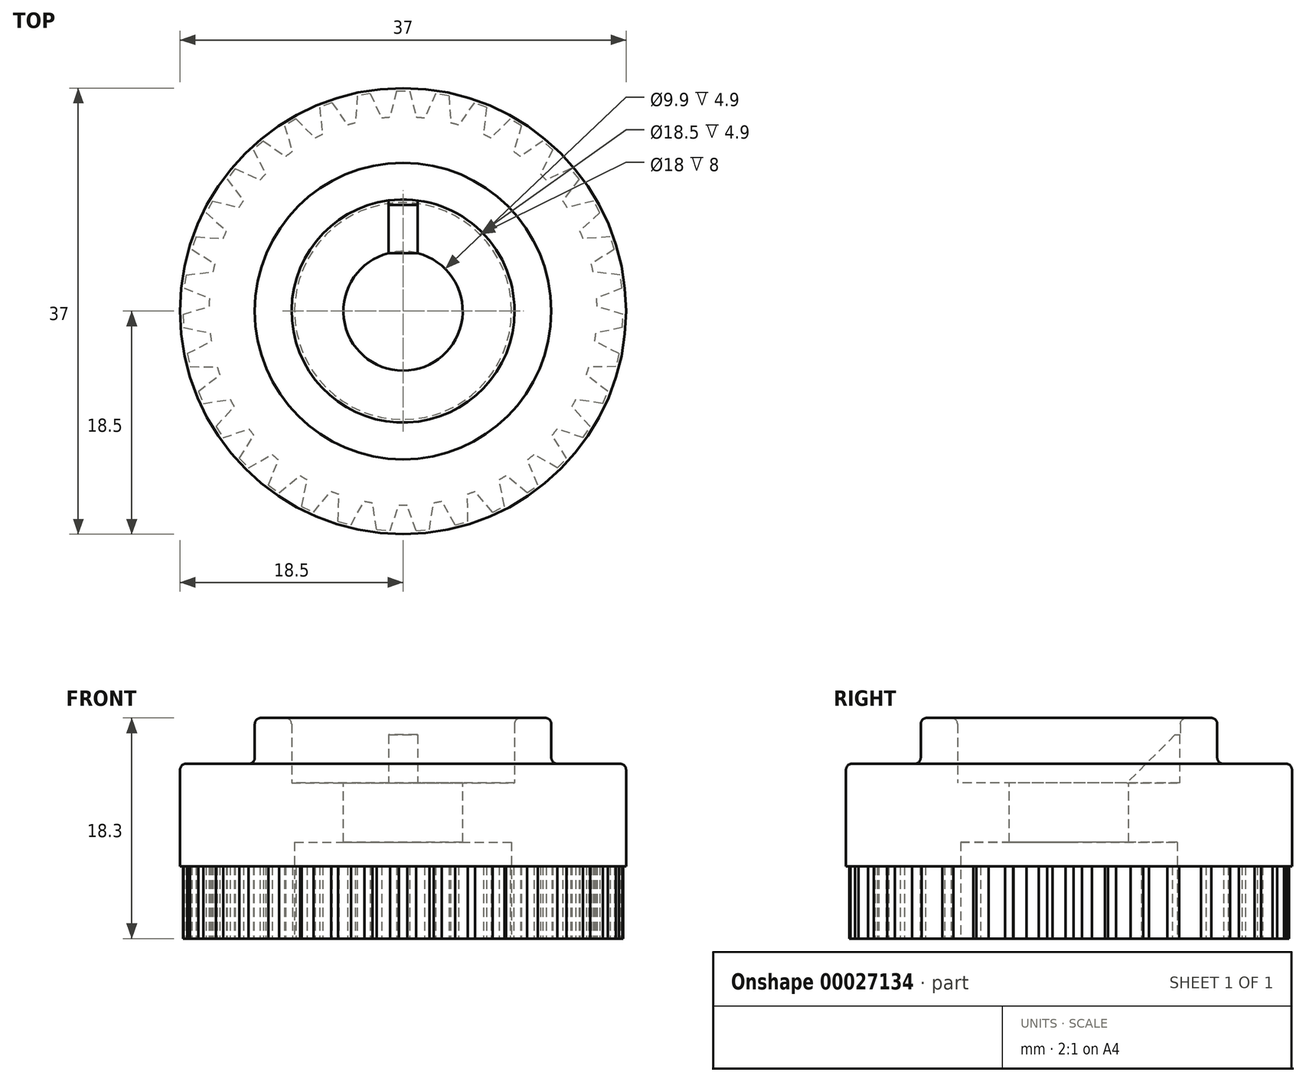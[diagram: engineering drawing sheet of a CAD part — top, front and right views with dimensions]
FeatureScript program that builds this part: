
annotation { "Feature Type Name" : "Feature", "Feature Type Description" : "" }
export const myFeature = defineFeature(function(context is Context, id is Id, definition is map)
    precondition{}
    {
        {
            var Q0;
            Q0=qCreatedBy(makeId("Top.planeOp"),FACE);
            var sketch = newSketch(context, id + "F0", { "sketchPlane" : qUnion([Q0])});
            skCircle(sketch, "E0", {"center": v(0, 0) * mm, "radius": 16.1 * mm});
            skLineSegment(sketch, "E1", {"start": v(0, 18.25) * mm, "end": v(0.55, 18.25) * mm});
            skLineSegment(sketch, "E2", {"start": v(0.55, 18.25) * mm, "end": v(1.1, 16.06) * mm});
            skLineSegment(sketch, "E3.MirrorCS", {"start": v(0, 18.25) * mm, "end": v(-0.55, 18.25) * mm});
            skLineSegment(sketch, "E4.MirrorCS", {"start": v(-0.55, 18.25) * mm, "end": v(-1.1, 16.06) * mm});
            skLineSegment(sketch, "E5.1.0", {"start": v(-3.26, 17.96) * mm, "end": v(-3.8, 17.86) * mm});
            skLineSegment(sketch, "E5.1.1", {"start": v(-3.26, 17.96) * mm, "end": v(-2.72, 18.05) * mm});
            skLineSegment(sketch, "E5.1.2", {"start": v(-3.8, 17.86) * mm, "end": v(-3.95, 15.6) * mm});
            skLineSegment(sketch, "E5.1.3", {"start": v(-2.72, 18.05) * mm, "end": v(-1.79, 16) * mm});
            skLineSegment(sketch, "E5.2.0", {"start": v(-6.41, 17.09) * mm, "end": v(-6.93, 16.9) * mm});
            skLineSegment(sketch, "E5.2.1", {"start": v(-6.41, 17.09) * mm, "end": v(-5.9, 17.28) * mm});
            skLineSegment(sketch, "E5.2.2", {"start": v(-6.93, 16.9) * mm, "end": v(-6.67, 14.65) * mm});
            skLineSegment(sketch, "E5.2.3", {"start": v(-5.9, 17.28) * mm, "end": v(-4.61, 15.42) * mm});
            skLineSegment(sketch, "E6.2.3.0", {"start": v(-9.36, 15.67) * mm, "end": v(-9.83, 15.38) * mm});
            skLineSegment(sketch, "E6.3.3.0", {"start": v(-9.36, 15.67) * mm, "end": v(-8.89, 15.95) * mm});
            skLineSegment(sketch, "E6.6.3.0", {"start": v(-9.83, 15.38) * mm, "end": v(-9.18, 13.22) * mm});
            skLineSegment(sketch, "E6.9.3.0", {"start": v(-8.89, 15.95) * mm, "end": v(-7.3, 14.35) * mm});
            skLineSegment(sketch, "E6.2.4.0", {"start": v(-12, 13.74) * mm, "end": v(-12.42, 13.38) * mm});
            skLineSegment(sketch, "E6.3.4.0", {"start": v(-12, 13.74) * mm, "end": v(-11.6, 14.1) * mm});
            skLineSegment(sketch, "E6.6.4.0", {"start": v(-12.42, 13.38) * mm, "end": v(-11.4, 11.37) * mm});
            skLineSegment(sketch, "E6.9.4.0", {"start": v(-11.6, 14.1) * mm, "end": v(-9.74, 12.82) * mm});
            skLineSegment(sketch, "E6.2.5.0", {"start": v(-14.27, 11.38) * mm, "end": v(-14.61, 10.95) * mm});
            skLineSegment(sketch, "E6.3.5.0", {"start": v(-14.27, 11.38) * mm, "end": v(-13.93, 11.8) * mm});
            skLineSegment(sketch, "E6.6.5.0", {"start": v(-14.61, 10.95) * mm, "end": v(-13.24, 9.15) * mm});
            skLineSegment(sketch, "E6.9.5.0", {"start": v(-13.93, 11.8) * mm, "end": v(-11.87, 10.87) * mm});
            skLineSegment(sketch, "E6.2.6.0", {"start": v(-16.07, 8.65) * mm, "end": v(-16.33, 8.16) * mm});
            skLineSegment(sketch, "E6.3.6.0", {"start": v(-16.07, 8.65) * mm, "end": v(-15.81, 9.13) * mm});
            skLineSegment(sketch, "E6.6.6.0", {"start": v(-16.33, 8.16) * mm, "end": v(-14.67, 6.64) * mm});
            skLineSegment(sketch, "E6.9.6.0", {"start": v(-15.81, 9.13) * mm, "end": v(-13.62, 8.58) * mm});
            skLineSegment(sketch, "E6.2.7.0", {"start": v(-17.36, 5.64) * mm, "end": v(-17.53, 5.12) * mm});
            skLineSegment(sketch, "E6.3.7.0", {"start": v(-17.36, 5.64) * mm, "end": v(-17.19, 6.16) * mm});
            skLineSegment(sketch, "E6.6.7.0", {"start": v(-17.53, 5.12) * mm, "end": v(-15.62, 3.92) * mm});
            skLineSegment(sketch, "E6.9.7.0", {"start": v(-17.19, 6.16) * mm, "end": v(-14.94, 6) * mm});
            skLineSegment(sketch, "E6.2.8.0", {"start": v(-18.08, 2.45) * mm, "end": v(-18.16, 1.9) * mm});
            skLineSegment(sketch, "E6.3.8.0", {"start": v(-18.08, 2.45) * mm, "end": v(-18.01, 3) * mm});
            skLineSegment(sketch, "E6.6.8.0", {"start": v(-18.16, 1.9) * mm, "end": v(-16.06, 1.07) * mm});
            skLineSegment(sketch, "E6.9.8.0", {"start": v(-18.01, 3) * mm, "end": v(-15.77, 3.25) * mm});
            skLineSegment(sketch, "E6.2.9.0", {"start": v(-18.23, -0.82) * mm, "end": v(-18.2, -1.37) * mm});
            skLineSegment(sketch, "E6.3.9.0", {"start": v(-18.23, -0.82) * mm, "end": v(-18.26, -0.27) * mm});
            skLineSegment(sketch, "E6.6.9.0", {"start": v(-18.2, -1.37) * mm, "end": v(-16, -1.82) * mm});
            skLineSegment(sketch, "E6.9.9.0", {"start": v(-18.26, -0.27) * mm, "end": v(-16.1, 0.38) * mm});
            skLineSegment(sketch, "E6.2.10.0", {"start": v(-17.8, -4.06) * mm, "end": v(-17.67, -4.6) * mm});
            skLineSegment(sketch, "E6.3.10.0", {"start": v(-17.8, -4.06) * mm, "end": v(-17.91, -3.52) * mm});
            skLineSegment(sketch, "E6.6.10.0", {"start": v(-17.67, -4.6) * mm, "end": v(-15.41, -4.65) * mm});
            skLineSegment(sketch, "E6.9.10.0", {"start": v(-17.91, -3.52) * mm, "end": v(-15.9, -2.5) * mm});
            skLineSegment(sketch, "E6.2.11.0", {"start": v(-16.78, -7.17) * mm, "end": v(-16.57, -7.68) * mm});
            skLineSegment(sketch, "E6.3.11.0", {"start": v(-16.78, -7.17) * mm, "end": v(-17, -6.67) * mm});
            skLineSegment(sketch, "E6.6.11.0", {"start": v(-16.57, -7.68) * mm, "end": v(-14.34, -7.32) * mm});
            skLineSegment(sketch, "E6.9.11.0", {"start": v(-17, -6.67) * mm, "end": v(-15.2, -5.3) * mm});
            skLineSegment(sketch, "E6.2.12.0", {"start": v(-15.23, -10.05) * mm, "end": v(-14.93, -10.51) * mm});
            skLineSegment(sketch, "E6.3.12.0", {"start": v(-15.23, -10.05) * mm, "end": v(-15.53, -9.6) * mm});
            skLineSegment(sketch, "E6.6.12.0", {"start": v(-14.93, -10.51) * mm, "end": v(-12.8, -9.77) * mm});
            skLineSegment(sketch, "E6.9.12.0", {"start": v(-15.53, -9.6) * mm, "end": v(-14.01, -7.93) * mm});
            skLineSegment(sketch, "E6.2.13.0", {"start": v(-13.2, -12.61) * mm, "end": v(-12.81, -13) * mm});
            skLineSegment(sketch, "E6.3.13.0", {"start": v(-13.2, -12.61) * mm, "end": v(-13.57, -12.21) * mm});
            skLineSegment(sketch, "E6.6.13.0", {"start": v(-12.81, -13) * mm, "end": v(-10.85, -11.9) * mm});
            skLineSegment(sketch, "E6.9.13.0", {"start": v(-13.57, -12.21) * mm, "end": v(-12.37, -10.3) * mm});
            skLineSegment(sketch, "E6.2.14.0", {"start": v(-10.73, -14.76) * mm, "end": v(-10.28, -15.09) * mm});
            skLineSegment(sketch, "E6.3.14.0", {"start": v(-10.73, -14.76) * mm, "end": v(-11.17, -14.44) * mm});
            skLineSegment(sketch, "E6.6.14.0", {"start": v(-10.28, -15.09) * mm, "end": v(-8.55, -13.64) * mm});
            skLineSegment(sketch, "E6.9.14.0", {"start": v(-11.17, -14.44) * mm, "end": v(-10.33, -12.35) * mm});
            skLineSegment(sketch, "E6.2.15.0", {"start": v(-7.92, -16.44) * mm, "end": v(-7.42, -16.68) * mm});
            skLineSegment(sketch, "E6.3.15.0", {"start": v(-7.92, -16.44) * mm, "end": v(-8.41, -16.2) * mm});
            skLineSegment(sketch, "E6.6.15.0", {"start": v(-7.42, -16.68) * mm, "end": v(-5.98, -14.95) * mm});
            skLineSegment(sketch, "E6.9.15.0", {"start": v(-8.41, -16.2) * mm, "end": v(-7.96, -14) * mm});
            skLineSegment(sketch, "E6.2.16.0", {"start": v(-4.86, -17.6) * mm, "end": v(-4.32, -17.74) * mm});
            skLineSegment(sketch, "E6.3.16.0", {"start": v(-4.86, -17.6) * mm, "end": v(-5.39, -17.45) * mm});
            skLineSegment(sketch, "E6.6.16.0", {"start": v(-4.32, -17.74) * mm, "end": v(-3.21, -15.78) * mm});
            skLineSegment(sketch, "E6.9.16.0", {"start": v(-5.39, -17.45) * mm, "end": v(-5.33, -15.2) * mm});
            skLineSegment(sketch, "E6.2.17.0", {"start": v(-1.64, -18.18) * mm, "end": v(-1.09, -18.23) * mm});
            skLineSegment(sketch, "E6.3.17.0", {"start": v(-1.64, -18.18) * mm, "end": v(-2.18, -18.13) * mm});
            skLineSegment(sketch, "E6.6.17.0", {"start": v(-1.09, -18.23) * mm, "end": v(-0.34, -16.1) * mm});
            skLineSegment(sketch, "E6.9.17.0", {"start": v(-2.18, -18.13) * mm, "end": v(-2.54, -15.9) * mm});
            skLineSegment(sketch, "E6.2.18.0", {"start": v(1.64, -18.18) * mm, "end": v(2.18, -18.13) * mm});
            skLineSegment(sketch, "E6.3.18.0", {"start": v(1.64, -18.18) * mm, "end": v(1.09, -18.23) * mm});
            skLineSegment(sketch, "E6.6.18.0", {"start": v(2.18, -18.13) * mm, "end": v(2.54, -15.9) * mm});
            skLineSegment(sketch, "E6.9.18.0", {"start": v(1.09, -18.23) * mm, "end": v(0.34, -16.1) * mm});
            skLineSegment(sketch, "E6.2.19.0", {"start": v(4.86, -17.6) * mm, "end": v(5.39, -17.45) * mm});
            skLineSegment(sketch, "E6.3.19.0", {"start": v(4.86, -17.6) * mm, "end": v(4.32, -17.74) * mm});
            skLineSegment(sketch, "E6.6.19.0", {"start": v(5.39, -17.45) * mm, "end": v(5.33, -15.2) * mm});
            skLineSegment(sketch, "E6.9.19.0", {"start": v(4.32, -17.74) * mm, "end": v(3.21, -15.78) * mm});
            skLineSegment(sketch, "E6.2.20.0", {"start": v(7.92, -16.44) * mm, "end": v(8.41, -16.2) * mm});
            skLineSegment(sketch, "E6.3.20.0", {"start": v(7.92, -16.44) * mm, "end": v(7.42, -16.68) * mm});
            skLineSegment(sketch, "E6.6.20.0", {"start": v(8.41, -16.2) * mm, "end": v(7.96, -14) * mm});
            skLineSegment(sketch, "E6.9.20.0", {"start": v(7.42, -16.68) * mm, "end": v(5.98, -14.95) * mm});
            skLineSegment(sketch, "E6.2.21.0", {"start": v(10.73, -14.76) * mm, "end": v(11.17, -14.44) * mm});
            skLineSegment(sketch, "E6.3.21.0", {"start": v(10.73, -14.76) * mm, "end": v(10.28, -15.09) * mm});
            skLineSegment(sketch, "E6.6.21.0", {"start": v(11.17, -14.44) * mm, "end": v(10.33, -12.35) * mm});
            skLineSegment(sketch, "E6.9.21.0", {"start": v(10.28, -15.09) * mm, "end": v(8.55, -13.64) * mm});
            skLineSegment(sketch, "E6.2.22.0", {"start": v(13.2, -12.61) * mm, "end": v(13.57, -12.21) * mm});
            skLineSegment(sketch, "E6.3.22.0", {"start": v(13.2, -12.61) * mm, "end": v(12.81, -13) * mm});
            skLineSegment(sketch, "E6.6.22.0", {"start": v(13.57, -12.21) * mm, "end": v(12.37, -10.3) * mm});
            skLineSegment(sketch, "E6.9.22.0", {"start": v(12.81, -13) * mm, "end": v(10.85, -11.9) * mm});
            skLineSegment(sketch, "E6.2.23.0", {"start": v(15.23, -10.05) * mm, "end": v(15.53, -9.6) * mm});
            skLineSegment(sketch, "E6.3.23.0", {"start": v(15.23, -10.05) * mm, "end": v(14.93, -10.51) * mm});
            skLineSegment(sketch, "E6.6.23.0", {"start": v(15.53, -9.6) * mm, "end": v(14.01, -7.93) * mm});
            skLineSegment(sketch, "E6.9.23.0", {"start": v(14.93, -10.51) * mm, "end": v(12.8, -9.77) * mm});
            skLineSegment(sketch, "E6.2.24.0", {"start": v(16.78, -7.17) * mm, "end": v(17, -6.67) * mm});
            skLineSegment(sketch, "E6.3.24.0", {"start": v(16.78, -7.17) * mm, "end": v(16.57, -7.68) * mm});
            skLineSegment(sketch, "E6.6.24.0", {"start": v(17, -6.67) * mm, "end": v(15.2, -5.3) * mm});
            skLineSegment(sketch, "E6.9.24.0", {"start": v(16.57, -7.68) * mm, "end": v(14.34, -7.32) * mm});
            skLineSegment(sketch, "E6.2.25.0", {"start": v(17.8, -4.06) * mm, "end": v(17.91, -3.52) * mm});
            skLineSegment(sketch, "E6.3.25.0", {"start": v(17.8, -4.06) * mm, "end": v(17.67, -4.6) * mm});
            skLineSegment(sketch, "E6.6.25.0", {"start": v(17.91, -3.52) * mm, "end": v(15.9, -2.5) * mm});
            skLineSegment(sketch, "E6.9.25.0", {"start": v(17.67, -4.6) * mm, "end": v(15.41, -4.65) * mm});
            skLineSegment(sketch, "E6.2.26.0", {"start": v(18.23, -0.82) * mm, "end": v(18.26, -0.27) * mm});
            skLineSegment(sketch, "E6.3.26.0", {"start": v(18.23, -0.82) * mm, "end": v(18.2, -1.37) * mm});
            skLineSegment(sketch, "E6.6.26.0", {"start": v(18.26, -0.27) * mm, "end": v(16.1, 0.38) * mm});
            skLineSegment(sketch, "E6.9.26.0", {"start": v(18.2, -1.37) * mm, "end": v(16, -1.82) * mm});
            skLineSegment(sketch, "E6.2.27.0", {"start": v(18.08, 2.45) * mm, "end": v(18.01, 3) * mm});
            skLineSegment(sketch, "E6.3.27.0", {"start": v(18.08, 2.45) * mm, "end": v(18.16, 1.9) * mm});
            skLineSegment(sketch, "E6.6.27.0", {"start": v(18.01, 3) * mm, "end": v(15.77, 3.25) * mm});
            skLineSegment(sketch, "E6.9.27.0", {"start": v(18.16, 1.9) * mm, "end": v(16.06, 1.07) * mm});
            skLineSegment(sketch, "E6.2.28.0", {"start": v(17.36, 5.64) * mm, "end": v(17.19, 6.16) * mm});
            skLineSegment(sketch, "E6.3.28.0", {"start": v(17.36, 5.64) * mm, "end": v(17.53, 5.12) * mm});
            skLineSegment(sketch, "E6.6.28.0", {"start": v(17.19, 6.16) * mm, "end": v(14.94, 6) * mm});
            skLineSegment(sketch, "E6.9.28.0", {"start": v(17.53, 5.12) * mm, "end": v(15.62, 3.92) * mm});
            skLineSegment(sketch, "E6.2.29.0", {"start": v(16.07, 8.65) * mm, "end": v(15.81, 9.13) * mm});
            skLineSegment(sketch, "E6.3.29.0", {"start": v(16.07, 8.65) * mm, "end": v(16.33, 8.16) * mm});
            skLineSegment(sketch, "E6.6.29.0", {"start": v(15.81, 9.13) * mm, "end": v(13.62, 8.58) * mm});
            skLineSegment(sketch, "E6.9.29.0", {"start": v(16.33, 8.16) * mm, "end": v(14.67, 6.64) * mm});
            skLineSegment(sketch, "E6.2.30.0", {"start": v(14.27, 11.38) * mm, "end": v(13.93, 11.8) * mm});
            skLineSegment(sketch, "E6.3.30.0", {"start": v(14.27, 11.38) * mm, "end": v(14.61, 10.95) * mm});
            skLineSegment(sketch, "E6.6.30.0", {"start": v(13.93, 11.8) * mm, "end": v(11.87, 10.87) * mm});
            skLineSegment(sketch, "E6.9.30.0", {"start": v(14.61, 10.95) * mm, "end": v(13.24, 9.15) * mm});
            skLineSegment(sketch, "E6.2.31.0", {"start": v(12, 13.74) * mm, "end": v(11.6, 14.1) * mm});
            skLineSegment(sketch, "E6.3.31.0", {"start": v(12, 13.74) * mm, "end": v(12.42, 13.38) * mm});
            skLineSegment(sketch, "E6.6.31.0", {"start": v(11.6, 14.1) * mm, "end": v(9.74, 12.82) * mm});
            skLineSegment(sketch, "E6.9.31.0", {"start": v(12.42, 13.38) * mm, "end": v(11.4, 11.37) * mm});
            skLineSegment(sketch, "E6.2.32.0", {"start": v(9.36, 15.67) * mm, "end": v(8.89, 15.95) * mm});
            skLineSegment(sketch, "E6.3.32.0", {"start": v(9.36, 15.67) * mm, "end": v(9.83, 15.38) * mm});
            skLineSegment(sketch, "E6.6.32.0", {"start": v(8.89, 15.95) * mm, "end": v(7.3, 14.35) * mm});
            skLineSegment(sketch, "E6.9.32.0", {"start": v(9.83, 15.38) * mm, "end": v(9.18, 13.22) * mm});
            skLineSegment(sketch, "E6.2.33.0", {"start": v(6.41, 17.09) * mm, "end": v(5.9, 17.28) * mm});
            skLineSegment(sketch, "E6.3.33.0", {"start": v(6.41, 17.09) * mm, "end": v(6.93, 16.9) * mm});
            skLineSegment(sketch, "E6.6.33.0", {"start": v(5.9, 17.28) * mm, "end": v(4.61, 15.42) * mm});
            skLineSegment(sketch, "E6.9.33.0", {"start": v(6.93, 16.9) * mm, "end": v(6.67, 14.65) * mm});
            skLineSegment(sketch, "E6.2.34.0", {"start": v(3.26, 17.96) * mm, "end": v(2.72, 18.05) * mm});
            skLineSegment(sketch, "E6.3.34.0", {"start": v(3.26, 17.96) * mm, "end": v(3.8, 17.86) * mm});
            skLineSegment(sketch, "E6.6.34.0", {"start": v(2.72, 18.05) * mm, "end": v(1.79, 16) * mm});
            skLineSegment(sketch, "E6.9.34.0", {"start": v(3.8, 17.86) * mm, "end": v(3.95, 15.6) * mm});
            skSolve(sketch);
        }
        {
            var Q0;
            Q0 = qSketchRegion(id + "F0", true);
            extrude(context, id + "F1", {"entities" : qUnion([Q0]), "depth" : 6 * mm});
        }
        {
            var Q0;
            Q0=makeQuery(id+"F1.opExtrude","CAP_FACE",FACE,{"disambiguationData":[OSD([sQuery(id+"F0.wireOp",EDGE,"E0"),sQuery(id+"F0.wireOp",EDGE,"E1"),sQuery(id+"F0.wireOp",EDGE,"E2"),sQuery(id+"F0.wireOp",EDGE,"E3.MirrorCS"),sQuery(id+"F0.wireOp",EDGE,"E4.MirrorCS"),sQuery(id+"F0.wireOp",EDGE,"E5.1.0"),sQuery(id+"F0.wireOp",EDGE,"E5.1.1"),sQuery(id+"F0.wireOp",EDGE,"E5.1.2"),sQuery(id+"F0.wireOp",EDGE,"E5.1.3"),sQuery(id+"F0.wireOp",EDGE,"E5.2.0"),sQuery(id+"F0.wireOp",EDGE,"E5.2.1"),sQuery(id+"F0.wireOp",EDGE,"E5.2.2"),sQuery(id+"F0.wireOp",EDGE,"E5.2.3"),sQuery(id+"F0.wireOp",EDGE,"E6.2.3.0"),sQuery(id+"F0.wireOp",EDGE,"E6.3.3.0"),sQuery(id+"F0.wireOp",EDGE,"E6.6.3.0"),sQuery(id+"F0.wireOp",EDGE,"E6.9.3.0"),sQuery(id+"F0.wireOp",EDGE,"E6.2.4.0"),sQuery(id+"F0.wireOp",EDGE,"E6.3.4.0"),sQuery(id+"F0.wireOp",EDGE,"E6.6.4.0"),sQuery(id+"F0.wireOp",EDGE,"E6.9.4.0"),sQuery(id+"F0.wireOp",EDGE,"E6.2.5.0"),sQuery(id+"F0.wireOp",EDGE,"E6.3.5.0"),sQuery(id+"F0.wireOp",EDGE,"E6.6.5.0"),sQuery(id+"F0.wireOp",EDGE,"E6.9.5.0"),sQuery(id+"F0.wireOp",EDGE,"E6.2.6.0"),sQuery(id+"F0.wireOp",EDGE,"E6.3.6.0"),sQuery(id+"F0.wireOp",EDGE,"E6.6.6.0"),sQuery(id+"F0.wireOp",EDGE,"E6.9.6.0"),sQuery(id+"F0.wireOp",EDGE,"E6.2.7.0"),sQuery(id+"F0.wireOp",EDGE,"E6.3.7.0"),sQuery(id+"F0.wireOp",EDGE,"E6.6.7.0"),sQuery(id+"F0.wireOp",EDGE,"E6.9.7.0"),sQuery(id+"F0.wireOp",EDGE,"E6.2.8.0"),sQuery(id+"F0.wireOp",EDGE,"E6.3.8.0"),sQuery(id+"F0.wireOp",EDGE,"E6.6.8.0"),sQuery(id+"F0.wireOp",EDGE,"E6.9.8.0"),sQuery(id+"F0.wireOp",EDGE,"E6.2.9.0"),sQuery(id+"F0.wireOp",EDGE,"E6.3.9.0"),sQuery(id+"F0.wireOp",EDGE,"E6.6.9.0"),sQuery(id+"F0.wireOp",EDGE,"E6.9.9.0"),sQuery(id+"F0.wireOp",EDGE,"E6.2.10.0"),sQuery(id+"F0.wireOp",EDGE,"E6.3.10.0"),sQuery(id+"F0.wireOp",EDGE,"E6.6.10.0"),sQuery(id+"F0.wireOp",EDGE,"E6.9.10.0"),sQuery(id+"F0.wireOp",EDGE,"E6.2.11.0"),sQuery(id+"F0.wireOp",EDGE,"E6.3.11.0"),sQuery(id+"F0.wireOp",EDGE,"E6.6.11.0"),sQuery(id+"F0.wireOp",EDGE,"E6.9.11.0"),sQuery(id+"F0.wireOp",EDGE,"E6.2.12.0"),sQuery(id+"F0.wireOp",EDGE,"E6.3.12.0"),sQuery(id+"F0.wireOp",EDGE,"E6.6.12.0"),sQuery(id+"F0.wireOp",EDGE,"E6.9.12.0"),sQuery(id+"F0.wireOp",EDGE,"E6.2.13.0"),sQuery(id+"F0.wireOp",EDGE,"E6.3.13.0"),sQuery(id+"F0.wireOp",EDGE,"E6.6.13.0"),sQuery(id+"F0.wireOp",EDGE,"E6.9.13.0"),sQuery(id+"F0.wireOp",EDGE,"E6.2.14.0"),sQuery(id+"F0.wireOp",EDGE,"E6.3.14.0"),sQuery(id+"F0.wireOp",EDGE,"E6.6.14.0"),sQuery(id+"F0.wireOp",EDGE,"E6.9.14.0"),sQuery(id+"F0.wireOp",EDGE,"E6.2.15.0"),sQuery(id+"F0.wireOp",EDGE,"E6.3.15.0"),sQuery(id+"F0.wireOp",EDGE,"E6.6.15.0"),sQuery(id+"F0.wireOp",EDGE,"E6.9.15.0"),sQuery(id+"F0.wireOp",EDGE,"E6.2.16.0"),sQuery(id+"F0.wireOp",EDGE,"E6.3.16.0"),sQuery(id+"F0.wireOp",EDGE,"E6.6.16.0"),sQuery(id+"F0.wireOp",EDGE,"E6.9.16.0"),sQuery(id+"F0.wireOp",EDGE,"E6.2.17.0"),sQuery(id+"F0.wireOp",EDGE,"E6.3.17.0"),sQuery(id+"F0.wireOp",EDGE,"E6.6.17.0"),sQuery(id+"F0.wireOp",EDGE,"E6.9.17.0"),sQuery(id+"F0.wireOp",EDGE,"E6.2.18.0"),sQuery(id+"F0.wireOp",EDGE,"E6.3.18.0"),sQuery(id+"F0.wireOp",EDGE,"E6.6.18.0"),sQuery(id+"F0.wireOp",EDGE,"E6.9.18.0"),sQuery(id+"F0.wireOp",EDGE,"E6.2.19.0"),sQuery(id+"F0.wireOp",EDGE,"E6.3.19.0"),sQuery(id+"F0.wireOp",EDGE,"E6.6.19.0"),sQuery(id+"F0.wireOp",EDGE,"E6.9.19.0"),sQuery(id+"F0.wireOp",EDGE,"E6.2.20.0"),sQuery(id+"F0.wireOp",EDGE,"E6.3.20.0"),sQuery(id+"F0.wireOp",EDGE,"E6.6.20.0"),sQuery(id+"F0.wireOp",EDGE,"E6.9.20.0"),sQuery(id+"F0.wireOp",EDGE,"E6.2.21.0"),sQuery(id+"F0.wireOp",EDGE,"E6.3.21.0"),sQuery(id+"F0.wireOp",EDGE,"E6.6.21.0"),sQuery(id+"F0.wireOp",EDGE,"E6.9.21.0"),sQuery(id+"F0.wireOp",EDGE,"E6.2.22.0"),sQuery(id+"F0.wireOp",EDGE,"E6.3.22.0"),sQuery(id+"F0.wireOp",EDGE,"E6.6.22.0"),sQuery(id+"F0.wireOp",EDGE,"E6.9.22.0"),sQuery(id+"F0.wireOp",EDGE,"E6.2.23.0"),sQuery(id+"F0.wireOp",EDGE,"E6.3.23.0"),sQuery(id+"F0.wireOp",EDGE,"E6.6.23.0"),sQuery(id+"F0.wireOp",EDGE,"E6.9.23.0"),sQuery(id+"F0.wireOp",EDGE,"E6.2.24.0"),sQuery(id+"F0.wireOp",EDGE,"E6.3.24.0"),sQuery(id+"F0.wireOp",EDGE,"E6.6.24.0"),sQuery(id+"F0.wireOp",EDGE,"E6.9.24.0"),sQuery(id+"F0.wireOp",EDGE,"E6.2.25.0"),sQuery(id+"F0.wireOp",EDGE,"E6.3.25.0"),sQuery(id+"F0.wireOp",EDGE,"E6.6.25.0"),sQuery(id+"F0.wireOp",EDGE,"E6.9.25.0"),sQuery(id+"F0.wireOp",EDGE,"E6.2.26.0"),sQuery(id+"F0.wireOp",EDGE,"E6.3.26.0"),sQuery(id+"F0.wireOp",EDGE,"E6.6.26.0"),sQuery(id+"F0.wireOp",EDGE,"E6.9.26.0"),sQuery(id+"F0.wireOp",EDGE,"E6.2.27.0"),sQuery(id+"F0.wireOp",EDGE,"E6.3.27.0"),sQuery(id+"F0.wireOp",EDGE,"E6.6.27.0"),sQuery(id+"F0.wireOp",EDGE,"E6.9.27.0"),sQuery(id+"F0.wireOp",EDGE,"E6.2.28.0"),sQuery(id+"F0.wireOp",EDGE,"E6.3.28.0"),sQuery(id+"F0.wireOp",EDGE,"E6.6.28.0"),sQuery(id+"F0.wireOp",EDGE,"E6.9.28.0"),sQuery(id+"F0.wireOp",EDGE,"E6.2.29.0"),sQuery(id+"F0.wireOp",EDGE,"E6.3.29.0"),sQuery(id+"F0.wireOp",EDGE,"E6.6.29.0"),sQuery(id+"F0.wireOp",EDGE,"E6.9.29.0"),sQuery(id+"F0.wireOp",EDGE,"E6.2.30.0"),sQuery(id+"F0.wireOp",EDGE,"E6.3.30.0"),sQuery(id+"F0.wireOp",EDGE,"E6.6.30.0"),sQuery(id+"F0.wireOp",EDGE,"E6.9.30.0"),sQuery(id+"F0.wireOp",EDGE,"E6.2.31.0"),sQuery(id+"F0.wireOp",EDGE,"E6.3.31.0"),sQuery(id+"F0.wireOp",EDGE,"E6.6.31.0"),sQuery(id+"F0.wireOp",EDGE,"E6.9.31.0"),sQuery(id+"F0.wireOp",EDGE,"E6.2.32.0"),sQuery(id+"F0.wireOp",EDGE,"E6.3.32.0"),sQuery(id+"F0.wireOp",EDGE,"E6.6.32.0"),sQuery(id+"F0.wireOp",EDGE,"E6.9.32.0"),sQuery(id+"F0.wireOp",EDGE,"E6.2.33.0"),sQuery(id+"F0.wireOp",EDGE,"E6.3.33.0"),sQuery(id+"F0.wireOp",EDGE,"E6.6.33.0"),sQuery(id+"F0.wireOp",EDGE,"E6.9.33.0"),sQuery(id+"F0.wireOp",EDGE,"E6.2.34.0"),sQuery(id+"F0.wireOp",EDGE,"E6.3.34.0"),sQuery(id+"F0.wireOp",EDGE,"E6.6.34.0"),sQuery(id+"F0.wireOp",EDGE,"E6.9.34.0")])],"isStart":false});
            var sketch = newSketch(context, id + "F2", { "sketchPlane" : qUnion([Q0])});
            skCircle(sketch, "E7", {"center": v(0, 0) * mm, "radius": 18.5 * mm});
            skSolve(sketch);
        }
        {
            var Q0;
            Q0 = qSketchRegion(id + "F2", true);
            extrude(context, id + "F3", {"entities" : qUnion([Q0]), "operationType" : NewBodyOperationType.ADD, "depth" : 8.5 * mm});
        }
        {
            var Q0;
            Q0=makeQuery(id+"F3.opExtrude","CAP_FACE",FACE,{"disambiguationData":[OSD([sQuery(id+"F2.wireOp",EDGE,"E7")])],"isStart":false});
            var sketch = newSketch(context, id + "F4", { "sketchPlane" : qUnion([Q0])});
            skCircle(sketch, "E8", {"center": v(0, 0) * mm, "radius": 12.3 * mm});
            skCircle(sketch, "E9", {"center": v(0, 0) * mm, "radius": 9.25 * mm});
            skSolve(sketch);
        }
        {
            var Q0;
            Q0 = qSketchRegion(id + "F4", true);
            extrude(context, id + "F5", {"entities" : qUnion([Q0]), "operationType" : NewBodyOperationType.ADD, "depth" : 3.8 * mm});
        }
        {
            var Q0;
            Q0=makeQuery(id+"F5.boolean.opBoolean","SPLIT",FACE,{"disambiguationData":[TD([makeQuery(id+"F5.opExtrude","SWEPT_FACE",FACE,{"disambiguationData":[OSD([sQuery(id+"F4.wireOp",EDGE,"E9")])]})])],"derivedFrom":makeQuery(id+"F3.opExtrude","CAP_FACE",FACE,{"disambiguationData":[OSD([sQuery(id+"F2.wireOp",EDGE,"E7")])],"isStart":false})});
            extrude(context, id + "F6", {"entities" : qUnion([Q0]), "operationType" : NewBodyOperationType.REMOVE, "oppositeDirection" : true, "depth" : 1.6 * mm});
        }
        {
            var Q0;
            Q0=makeQuery(id+"F6.boolean.opBoolean","COPY",FACE,{"derivedFrom":makeQuery(id+"F6.opExtrude","CAP_FACE",FACE,{"disambiguationData":[OSD([sQuery(id+"F2.wireOp",EDGE,"E7")])],"isStart":false})});
            var sketch = newSketch(context, id + "F7", { "sketchPlane" : qUnion([Q0])});
            skCircle(sketch, "E10", {"center": v(0, 0) * mm, "radius": 4.95 * mm});
            skSolve(sketch);
        }
        {
            var Q0;
            Q0 = qSketchRegion(id + "F7", true);
            extrude(context, id + "F8", {"entities" : qUnion([Q0]), "operationType" : NewBodyOperationType.REMOVE, "endBound" : BoundingType.UP_TO_NEXT, "oppositeDirection" : true, "depth" : 25 * mm});
        }
        {
            var Q0;
            Q0=makeQuery(id+"F6.boolean.opBoolean","COPY",FACE,{"derivedFrom":makeQuery(id+"F6.opExtrude","CAP_FACE",FACE,{"disambiguationData":[OSD([sQuery(id+"F2.wireOp",EDGE,"E7")])],"isStart":false})});
            var sketch = newSketch(context, id + "F9", { "sketchPlane" : qUnion([Q0])});
            skLineSegment(sketch, "E11.rect.bottom", {"start": v(1.2, 4.8) * mm, "end": v(-1.2, 4.8) * mm});
            skLineSegment(sketch, "E11.rect.top", {"start": v(1.2, 9.25) * mm, "end": v(-1.2, 9.25) * mm});
            skLineSegment(sketch, "E11.rect.left", {"start": v(1.2, 4.8) * mm, "end": v(1.2, 9.25) * mm});
            skLineSegment(sketch, "E11.rect.right", {"start": v(-1.2, 4.8) * mm, "end": v(-1.2, 9.25) * mm});
            skPoint(sketch, "E11.rect.middle", {"position": v(0, 7.03) * mm});
            skSolve(sketch);
        }
        {
            var Q0;
            Q0 = qSketchRegion(id + "F9", true);
            extrude(context, id + "F10", {"entities" : qUnion([Q0]), "operationType" : NewBodyOperationType.ADD, "depth" : 4 * mm});
        }
        {
            var Q0;
            Q0=makeQuery(id+"F10.opExtrude","CAP_EDGE",EDGE,{"disambiguationData":[OSD([sQuery(id+"F9.wireOp",EDGE,"E11.rect.bottom")])],"isStart":false});
            chamfer(context, id + "F11", {"entities" : qUnion([Q0]), "width" : 4 * mm, "tangentPropagation" : true});
        }
        {
            var Q0;
            Q0=makeQuery(id+"F1.opExtrude","CAP_FACE",FACE,{"disambiguationData":[OSD([sQuery(id+"F0.wireOp",EDGE,"E0"),sQuery(id+"F0.wireOp",EDGE,"E1"),sQuery(id+"F0.wireOp",EDGE,"E2"),sQuery(id+"F0.wireOp",EDGE,"E3.MirrorCS"),sQuery(id+"F0.wireOp",EDGE,"E4.MirrorCS"),sQuery(id+"F0.wireOp",EDGE,"E5.1.0"),sQuery(id+"F0.wireOp",EDGE,"E5.1.1"),sQuery(id+"F0.wireOp",EDGE,"E5.1.2"),sQuery(id+"F0.wireOp",EDGE,"E5.1.3"),sQuery(id+"F0.wireOp",EDGE,"E5.2.0"),sQuery(id+"F0.wireOp",EDGE,"E5.2.1"),sQuery(id+"F0.wireOp",EDGE,"E5.2.2"),sQuery(id+"F0.wireOp",EDGE,"E5.2.3"),sQuery(id+"F0.wireOp",EDGE,"E6.2.3.0"),sQuery(id+"F0.wireOp",EDGE,"E6.3.3.0"),sQuery(id+"F0.wireOp",EDGE,"E6.6.3.0"),sQuery(id+"F0.wireOp",EDGE,"E6.9.3.0"),sQuery(id+"F0.wireOp",EDGE,"E6.2.4.0"),sQuery(id+"F0.wireOp",EDGE,"E6.3.4.0"),sQuery(id+"F0.wireOp",EDGE,"E6.6.4.0"),sQuery(id+"F0.wireOp",EDGE,"E6.9.4.0"),sQuery(id+"F0.wireOp",EDGE,"E6.2.5.0"),sQuery(id+"F0.wireOp",EDGE,"E6.3.5.0"),sQuery(id+"F0.wireOp",EDGE,"E6.6.5.0"),sQuery(id+"F0.wireOp",EDGE,"E6.9.5.0"),sQuery(id+"F0.wireOp",EDGE,"E6.2.6.0"),sQuery(id+"F0.wireOp",EDGE,"E6.3.6.0"),sQuery(id+"F0.wireOp",EDGE,"E6.6.6.0"),sQuery(id+"F0.wireOp",EDGE,"E6.9.6.0"),sQuery(id+"F0.wireOp",EDGE,"E6.2.7.0"),sQuery(id+"F0.wireOp",EDGE,"E6.3.7.0"),sQuery(id+"F0.wireOp",EDGE,"E6.6.7.0"),sQuery(id+"F0.wireOp",EDGE,"E6.9.7.0"),sQuery(id+"F0.wireOp",EDGE,"E6.2.8.0"),sQuery(id+"F0.wireOp",EDGE,"E6.3.8.0"),sQuery(id+"F0.wireOp",EDGE,"E6.6.8.0"),sQuery(id+"F0.wireOp",EDGE,"E6.9.8.0"),sQuery(id+"F0.wireOp",EDGE,"E6.2.9.0"),sQuery(id+"F0.wireOp",EDGE,"E6.3.9.0"),sQuery(id+"F0.wireOp",EDGE,"E6.6.9.0"),sQuery(id+"F0.wireOp",EDGE,"E6.9.9.0"),sQuery(id+"F0.wireOp",EDGE,"E6.2.10.0"),sQuery(id+"F0.wireOp",EDGE,"E6.3.10.0"),sQuery(id+"F0.wireOp",EDGE,"E6.6.10.0"),sQuery(id+"F0.wireOp",EDGE,"E6.9.10.0"),sQuery(id+"F0.wireOp",EDGE,"E6.2.11.0"),sQuery(id+"F0.wireOp",EDGE,"E6.3.11.0"),sQuery(id+"F0.wireOp",EDGE,"E6.6.11.0"),sQuery(id+"F0.wireOp",EDGE,"E6.9.11.0"),sQuery(id+"F0.wireOp",EDGE,"E6.2.12.0"),sQuery(id+"F0.wireOp",EDGE,"E6.3.12.0"),sQuery(id+"F0.wireOp",EDGE,"E6.6.12.0"),sQuery(id+"F0.wireOp",EDGE,"E6.9.12.0"),sQuery(id+"F0.wireOp",EDGE,"E6.2.13.0"),sQuery(id+"F0.wireOp",EDGE,"E6.3.13.0"),sQuery(id+"F0.wireOp",EDGE,"E6.6.13.0"),sQuery(id+"F0.wireOp",EDGE,"E6.9.13.0"),sQuery(id+"F0.wireOp",EDGE,"E6.2.14.0"),sQuery(id+"F0.wireOp",EDGE,"E6.3.14.0"),sQuery(id+"F0.wireOp",EDGE,"E6.6.14.0"),sQuery(id+"F0.wireOp",EDGE,"E6.9.14.0"),sQuery(id+"F0.wireOp",EDGE,"E6.2.15.0"),sQuery(id+"F0.wireOp",EDGE,"E6.3.15.0"),sQuery(id+"F0.wireOp",EDGE,"E6.6.15.0"),sQuery(id+"F0.wireOp",EDGE,"E6.9.15.0"),sQuery(id+"F0.wireOp",EDGE,"E6.2.16.0"),sQuery(id+"F0.wireOp",EDGE,"E6.3.16.0"),sQuery(id+"F0.wireOp",EDGE,"E6.6.16.0"),sQuery(id+"F0.wireOp",EDGE,"E6.9.16.0"),sQuery(id+"F0.wireOp",EDGE,"E6.2.17.0"),sQuery(id+"F0.wireOp",EDGE,"E6.3.17.0"),sQuery(id+"F0.wireOp",EDGE,"E6.6.17.0"),sQuery(id+"F0.wireOp",EDGE,"E6.9.17.0"),sQuery(id+"F0.wireOp",EDGE,"E6.2.18.0"),sQuery(id+"F0.wireOp",EDGE,"E6.3.18.0"),sQuery(id+"F0.wireOp",EDGE,"E6.6.18.0"),sQuery(id+"F0.wireOp",EDGE,"E6.9.18.0"),sQuery(id+"F0.wireOp",EDGE,"E6.2.19.0"),sQuery(id+"F0.wireOp",EDGE,"E6.3.19.0"),sQuery(id+"F0.wireOp",EDGE,"E6.6.19.0"),sQuery(id+"F0.wireOp",EDGE,"E6.9.19.0"),sQuery(id+"F0.wireOp",EDGE,"E6.2.20.0"),sQuery(id+"F0.wireOp",EDGE,"E6.3.20.0"),sQuery(id+"F0.wireOp",EDGE,"E6.6.20.0"),sQuery(id+"F0.wireOp",EDGE,"E6.9.20.0"),sQuery(id+"F0.wireOp",EDGE,"E6.2.21.0"),sQuery(id+"F0.wireOp",EDGE,"E6.3.21.0"),sQuery(id+"F0.wireOp",EDGE,"E6.6.21.0"),sQuery(id+"F0.wireOp",EDGE,"E6.9.21.0"),sQuery(id+"F0.wireOp",EDGE,"E6.2.22.0"),sQuery(id+"F0.wireOp",EDGE,"E6.3.22.0"),sQuery(id+"F0.wireOp",EDGE,"E6.6.22.0"),sQuery(id+"F0.wireOp",EDGE,"E6.9.22.0"),sQuery(id+"F0.wireOp",EDGE,"E6.2.23.0"),sQuery(id+"F0.wireOp",EDGE,"E6.3.23.0"),sQuery(id+"F0.wireOp",EDGE,"E6.6.23.0"),sQuery(id+"F0.wireOp",EDGE,"E6.9.23.0"),sQuery(id+"F0.wireOp",EDGE,"E6.2.24.0"),sQuery(id+"F0.wireOp",EDGE,"E6.3.24.0"),sQuery(id+"F0.wireOp",EDGE,"E6.6.24.0"),sQuery(id+"F0.wireOp",EDGE,"E6.9.24.0"),sQuery(id+"F0.wireOp",EDGE,"E6.2.25.0"),sQuery(id+"F0.wireOp",EDGE,"E6.3.25.0"),sQuery(id+"F0.wireOp",EDGE,"E6.6.25.0"),sQuery(id+"F0.wireOp",EDGE,"E6.9.25.0"),sQuery(id+"F0.wireOp",EDGE,"E6.2.26.0"),sQuery(id+"F0.wireOp",EDGE,"E6.3.26.0"),sQuery(id+"F0.wireOp",EDGE,"E6.6.26.0"),sQuery(id+"F0.wireOp",EDGE,"E6.9.26.0"),sQuery(id+"F0.wireOp",EDGE,"E6.2.27.0"),sQuery(id+"F0.wireOp",EDGE,"E6.3.27.0"),sQuery(id+"F0.wireOp",EDGE,"E6.6.27.0"),sQuery(id+"F0.wireOp",EDGE,"E6.9.27.0"),sQuery(id+"F0.wireOp",EDGE,"E6.2.28.0"),sQuery(id+"F0.wireOp",EDGE,"E6.3.28.0"),sQuery(id+"F0.wireOp",EDGE,"E6.6.28.0"),sQuery(id+"F0.wireOp",EDGE,"E6.9.28.0"),sQuery(id+"F0.wireOp",EDGE,"E6.2.29.0"),sQuery(id+"F0.wireOp",EDGE,"E6.3.29.0"),sQuery(id+"F0.wireOp",EDGE,"E6.6.29.0"),sQuery(id+"F0.wireOp",EDGE,"E6.9.29.0"),sQuery(id+"F0.wireOp",EDGE,"E6.2.30.0"),sQuery(id+"F0.wireOp",EDGE,"E6.3.30.0"),sQuery(id+"F0.wireOp",EDGE,"E6.6.30.0"),sQuery(id+"F0.wireOp",EDGE,"E6.9.30.0"),sQuery(id+"F0.wireOp",EDGE,"E6.2.31.0"),sQuery(id+"F0.wireOp",EDGE,"E6.3.31.0"),sQuery(id+"F0.wireOp",EDGE,"E6.6.31.0"),sQuery(id+"F0.wireOp",EDGE,"E6.9.31.0"),sQuery(id+"F0.wireOp",EDGE,"E6.2.32.0"),sQuery(id+"F0.wireOp",EDGE,"E6.3.32.0"),sQuery(id+"F0.wireOp",EDGE,"E6.6.32.0"),sQuery(id+"F0.wireOp",EDGE,"E6.9.32.0"),sQuery(id+"F0.wireOp",EDGE,"E6.2.33.0"),sQuery(id+"F0.wireOp",EDGE,"E6.3.33.0"),sQuery(id+"F0.wireOp",EDGE,"E6.6.33.0"),sQuery(id+"F0.wireOp",EDGE,"E6.9.33.0"),sQuery(id+"F0.wireOp",EDGE,"E6.2.34.0"),sQuery(id+"F0.wireOp",EDGE,"E6.3.34.0"),sQuery(id+"F0.wireOp",EDGE,"E6.6.34.0"),sQuery(id+"F0.wireOp",EDGE,"E6.9.34.0")])],"isStart":true});
            var sketch = newSketch(context, id + "F12", { "sketchPlane" : qUnion([Q0])});
            skCircle(sketch, "E12", {"center": v(0, 0) * mm, "radius": 9 * mm});
            skSolve(sketch);
        }
        {
            var Q0;
            Q0 = qSketchRegion(id + "F12", true);
            extrude(context, id + "F13", {"entities" : qUnion([Q0]), "operationType" : NewBodyOperationType.REMOVE, "oppositeDirection" : true, "depth" : 8 * mm});
        }
        {
            var Q0;
            Q0=makeQuery(id+"F13.boolean.opBoolean","COPY",EDGE,{"derivedFrom":makeQuery(id+"F13.opExtrude","CAP_EDGE",EDGE,{"disambiguationData":[OSD([sQuery(id+"F12.wireOp",EDGE,"E12")])],"isStart":true})});
            var Q1;
            Q1=makeQuery(id+"F5.opExtrude","CAP_EDGE",EDGE,{"disambiguationData":[OSD([sQuery(id+"F4.wireOp",EDGE,"E9")])],"isStart":false});
            var Q2;
            {var subQ0=sQuery(id+"F2.wireOp",EDGE,"E7");Q2=makeQuery(id+"F5.boolean.opBoolean","SPLIT",FACE,{"disambiguationData":[TD([makeQuery(id+"F3.opExtrude","SWEPT_FACE",FACE,{"disambiguationData":[OSD([subQ0])]})])],"derivedFrom":makeQuery(id+"F3.opExtrude","CAP_FACE",FACE,{"disambiguationData":[OSD([subQ0])],"isStart":false})});}
            var Q3;
            Q3=makeQuery(id+"F5.opExtrude","CAP_EDGE",EDGE,{"disambiguationData":[OSD([sQuery(id+"F4.wireOp",EDGE,"E8")])],"isStart":false});
            fillet(context, id + "F14", {"entities" : qUnion([Q0, Q1, Q2, Q3]), "radius" : .5 * mm, "tangentPropagation" : true, "allowEdgeOverflow" : false});
        }
    });
